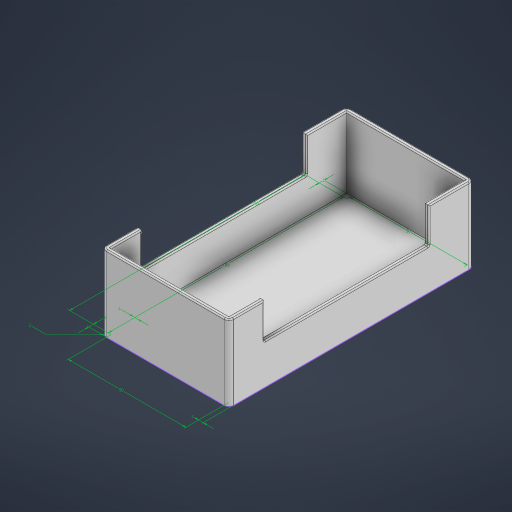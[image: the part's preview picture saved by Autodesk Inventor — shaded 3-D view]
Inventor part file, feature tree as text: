
AUTODESK INVENTOR PART (.ipt)
format: ipt  version: 2024.2 (Build 282272000, 272)  size: 288,768 bytes
history: native  units: mm
features: extrude x3, sketch x2, projected_geometry x2, fillet x1
ambient origin geometry x8: Origin, YZ Plane, XZ Plane, XY Plane, X Axis, Y Axis, Z Axis, Center Point
bodies: Solid1 (feature_tree)
feature tree (8):
  sketch  "Sketch1"  dims[d0=50.0mm d1=100.0mm]
  extrude  "Extrusion1"  Depth=100.0mm
  extrude  "Extrusion2"  Depth=100.0mm
  extrude  "Extrusion3"  Depth=2.0mm
  fillet  "Fillet1"  Radius=2.0mm
  sketch  "Sketch2"  dims[d7=2.0mm d8=100.0mm d9=2.0mm d10=2.0mm d11=2.0mm d12=2.0mm d13=50.0mm d14=2.0mm d15=0.0mm d16=32.0mm d17=0.0mm d18=2.0mm d19=70.0mm d20=50.0mm d21=15.0mm d22=0.0mm d23=0.5mm]
  projected_geometry  "Projected Loop1"
  projected_geometry  "Projected Loop2"
